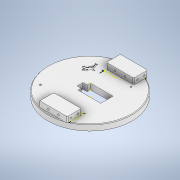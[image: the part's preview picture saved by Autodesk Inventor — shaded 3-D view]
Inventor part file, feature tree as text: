
AUTODESK INVENTOR PART (.ipt)
format: ipt  version: 2021 (Build 250183000, 183)  size: 552,448 bytes
history: native  units: mm
features: sketch x35, extrude x22, fillet x10, chamfer x2, other x1
ambient origin geometry x8: Origin, YZ Plane, XZ Plane, XY Plane, X Axis, Y Axis, Z Axis, Center Point
bodies: Body1 (feature_tree)
feature tree (70):
  other  "Sólido1"
  extrude  "Extrusión1"  Depth=20.0mm TaperAngle=0.0deg
  sketch  "Boceto2"  dims[d13=39.0mm d31=1.0mm d32=0.0mm]
  sketch  "Boceto3"  dims[d33=1.0mm d34=2.0mm d35=45.0deg d64=10.0mm d65=0.0mm d69=0.5mm d70=0.0mm]
  extrude  "Extrusión2"  Depth=1.0mm TaperAngle=0.0deg
  extrude  "Extrusión5"  Depth=10.0mm TaperAngle=0.0deg
  chamfer  "Chaflán1"  Distance=0.5mm
  sketch  "Boceto9"  dims[d79=1.6mm d80=45.4mm d81=1.6mm]
  sketch  "Boceto10"  dims[d82=12.0mm d83=0.5mm d84=0.0mm]
  sketch  "Boceto11"  dims[d85=1.0mm d92=10.5mm d93=0.0mm d94=32.5mm d95=0.0mm]
  extrude  "Extrusión6"  Depth=2.0mm TaperAngle=15.0deg
  extrude  "Extrusión7"  Depth=45.4mm
  fillet  "Empalme6"  Radius=1.6mm
  chamfer  "Chaflán2"  Distance=0.5mm
  sketch  "Boceto13"  dims[d99=12.75mm d101=6.4mm]
  extrude  "Extrusión8"  Depth=10.5mm TaperAngle=0.0deg
  fillet  "Empalme7"  Radius=32.5mm
  extrude  "Extrusión9"  Depth=10.0mm
  extrude  "Extrusión10"  Depth=6.4mm
  extrude  "Extrusión11"  Depth=10.0mm TaperAngle=0.0deg
  sketch  "Boceto18"  dims[d181=7.4mm d182=40.0mm d184=360.0deg]
  sketch  "Boceto19"  dims[d186=4.0mm d187=0.0mm d188=2.5mm]
  sketch  "Boceto20"  dims[d189=8.0mm d190=100.0mm d191=0.0mm]
  extrude  "Extrusión12"  Depth=4.0mm
  sketch  "Boceto22"  dims[d198=100.0mm d199=0.0mm d200=100.0mm d201=0.0mm]
  extrude  "Extrusión13"  Depth=1.0mm
  fillet  "Empalme8"  Radius=1.0mm
  fillet  "Empalme9"  Radius=1.0mm
  fillet  "Empalme10"  Radius=0.5mm
  fillet  "Empalme11"  [1 undecoded]
  fillet  "Empalme12"  Radius=0.2mm
  fillet  "Empalme13"  Radius=44.5mm
  sketch  "Boceto24"  dims[d230=15.0mm d231=15.0mm]
  extrude  "Extrusión17"  Depth=40.0mm TaperAngle=360.0deg
  extrude  "Extrusión18"  Depth=4.0mm
  extrude  "Extrusión19"  Depth=100.0mm TaperAngle=0.0deg
  extrude  "Extrusión20"  Depth=7.0mm
  fillet  "Empalme14"  Radius=10.0mm
  extrude  "Extrusión21"  Depth=100.0mm TaperAngle=0.0deg
  sketch  "Boceto32"  dims[d59=0.5mm]
  sketch  "Boceto33"  dims[d60=0.872665mm]
  extrude  "Extrusión22"  Depth=10.0mm TaperAngle=0.0deg
  sketch  "Boceto35"  dims[d62=0.872665mm]
  extrude  "Extrusión23"  Depth=15.0mm
  sketch  "Boceto37"  dims[d229=0.5mm]
  extrude  "Extrusión24"  Depth=5.0mm
  extrude  "Extrusión25"  Depth=3.0mm
  sketch  "Boceto40"
  extrude  "Extrusión26"  Depth=10.0mm TaperAngle=0.0deg
  fillet  "Empalme15"  Radius=2.0mm
  extrude  "Extrusión27"  Depth=10.0mm TaperAngle=0.0deg
  sketch  "Boceto1"  dims[d1=10.0mm d2=0.0mm d11=20.0mm d12=0.0mm]
  sketch  "Boceto4"  dims[d71=1.0mm d72=1.0mm d73=2.0mm d74=15.0deg]
  sketch  "Boceto12"  dims[d96=10.0mm d97=0.0mm d98=10.0mm]
  sketch  "Boceto14"  dims[d102=10.0mm d103=0.0mm d105=22.0mm d106=0.0mm]
  sketch  "Boceto15"  dims[d109=4.0mm d110=4.0mm]
  sketch  "Boceto16"  dims[d123=1.0mm d124=1.0mm d125=1.0mm d126=1.0mm]
  sketch  "Boceto17"  dims[d135=15.0mm d144=7.0mm d145=7.0mm d146=7.0mm d147=7.0mm d148=7.0mm d149=7.0mm d150=7.0mm d151=7.0mm d157=2.3mm d158=0.5mm d162=0.5mm d176=0.5mm d177=0.0mm d178=0.2mm d179=0.0mm d180=44.5mm]
  sketch  "Boceto21"  dims[d192=2.0mm d196=7.0mm d197=10.0mm]
  sketch  "Boceto23"  dims[d211=10.0mm d212=0.0mm d227=10.0mm d228=0.0mm]
  sketch  "Boceto28"  dims[d232=5.0mm d233=5.0mm]
  sketch  "Boceto29"  dims[d234=3.0mm d235=3.0mm]
  sketch  "Boceto30"  dims[d236=200.0mm d237=0.0mm d246=10.0mm d247=0.0mm d248=2.0mm]
  sketch  "Boceto31"  dims[d251=3.0mm d252=10.0mm d253=0.0mm]
  sketch  "Boceto34"  dims[d61=0.5mm]
  sketch  "Boceto36"  dims[d104=0.872665mm]
  sketch  "Boceto38"
  sketch  "Boceto39"
  sketch  "Boceto41"
  sketch  "Boceto42"
note: 1 required parameter value undecoded (feature->parameter linkage not recoverable at this tier; creation-order binding heuristic only, values carry confidence <= 0.55)
